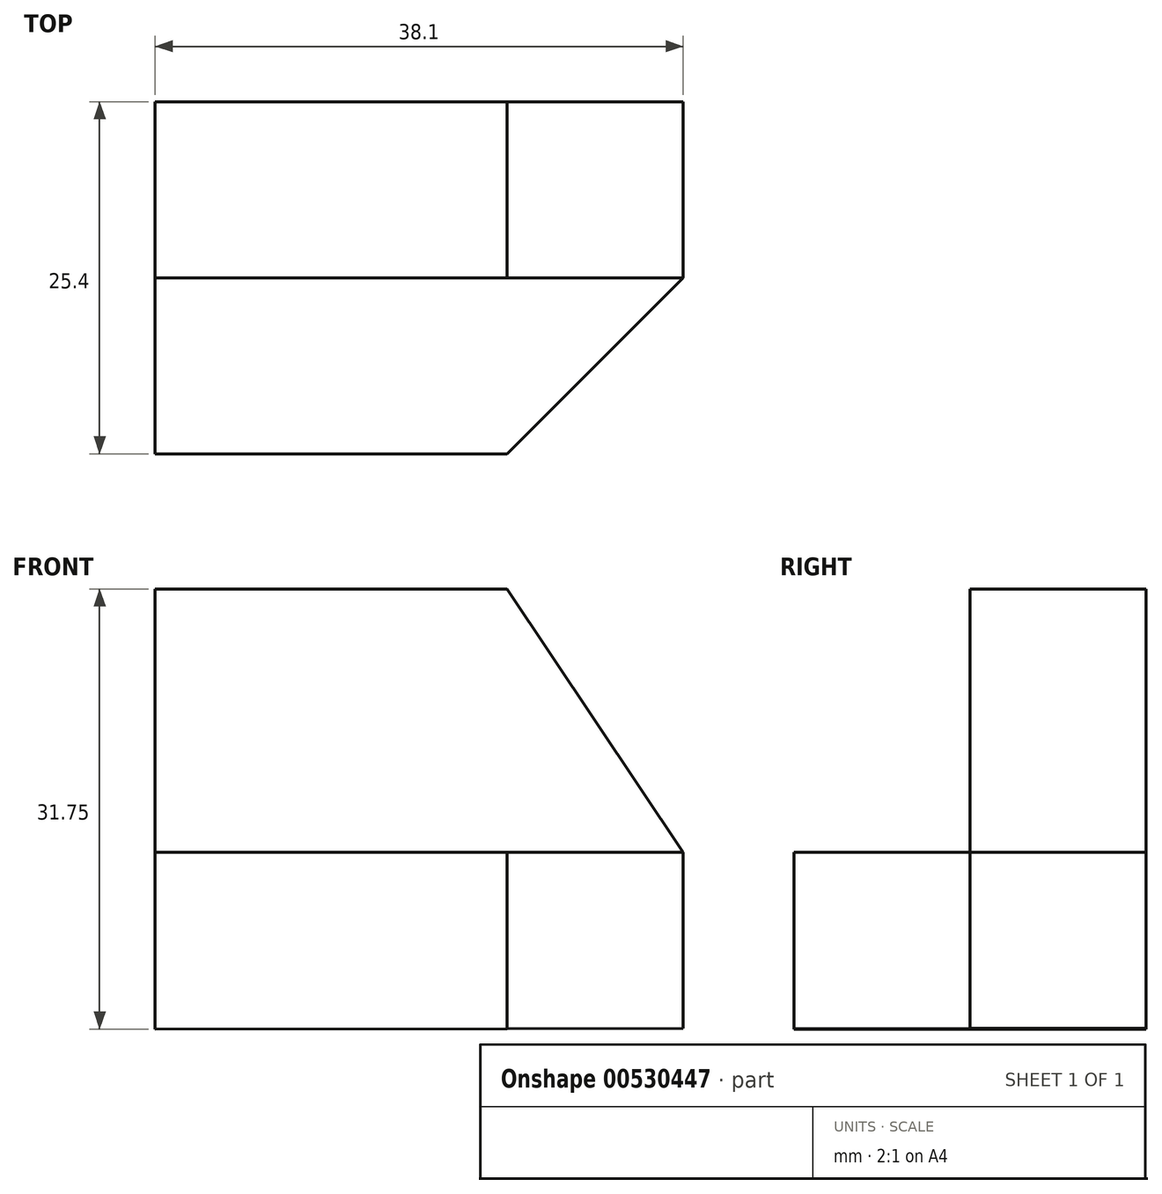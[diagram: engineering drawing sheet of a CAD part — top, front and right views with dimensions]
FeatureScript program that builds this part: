
annotation { "Feature Type Name" : "Feature", "Feature Type Description" : "" }
export const myFeature = defineFeature(function(context is Context, id is Id, definition is map)
    precondition{}
    {
        {
            var Q0;
            Q0=qCreatedBy(makeId("Front.planeOp"),FACE);
            var sketch = newSketch(context, id + "F0", { "sketchPlane" : qUnion([Q0])});
            skLineSegment(sketch, "E0", {"start": v(-69.66, 61.41) * mm, "end": v(-69.66, 29.66) * mm});
            skLineSegment(sketch, "E1", {"start": v(-69.66, 61.41) * mm, "end": v(-44.26, 61.41) * mm});
            skLineSegment(sketch, "E2", {"start": v(-44.26, 61.41) * mm, "end": v(-31.56, 42.4) * mm});
            skLineSegment(sketch, "E3", {"start": v(-31.56, 42.4) * mm, "end": v(-31.56, 29.7) * mm});
            skLineSegment(sketch, "E4", {"start": v(-31.56, 29.7) * mm, "end": v(-69.66, 29.66) * mm});
            skSolve(sketch);
        }
        {
            var Q0;
            Q0=makeQuery(id+"FoG6RG5lKM2hwuI_0.opExtrude","CAP_FACE",FACE,{"disambiguationData":[OSD([sQuery(id+"F0.wireOp",EDGE,"E0"),sQuery(id+"F0.wireOp",EDGE,"E1"),sQuery(id+"F0.wireOp",EDGE,"E2"),sQuery(id+"F0.wireOp",EDGE,"E3"),sQuery(id+"F0.wireOp",EDGE,"E4")])],"isStart":false});
            var sketch = newSketch(context, id + "F1", { "sketchPlane" : qUnion([Q0])});
            skLineSegment(sketch, "E5", {"start": v(-31.56, 29.7) * mm, "end": v(-31.56, 42.4) * mm});
            skLineSegment(sketch, "E6", {"start": v(-31.56, 42.4) * mm, "end": v(-69.66, 42.4) * mm});
            skLineSegment(sketch, "E7", {"start": v(-69.66, 42.4) * mm, "end": v(-69.66, 29.66) * mm});
            skLineSegment(sketch, "E8", {"start": v(-69.66, 29.66) * mm, "end": v(-31.56, 29.7) * mm});
            skSolve(sketch);
        }
        {
            var Q0;
            Q0=makeQuery(id+"FJzksTEYq52pJHC_0.opExtrude","CAP_FACE",FACE,{"disambiguationData":[OSD([sQuery(id+"F0.wireOp",EDGE,"E0"),sQuery(id+"F0.wireOp",EDGE,"E1"),sQuery(id+"F0.wireOp",EDGE,"E2"),sQuery(id+"F0.wireOp",EDGE,"E3"),sQuery(id+"F0.wireOp",EDGE,"E4")])],"isStart":false});
            var sketch = newSketch(context, id + "F2", { "sketchPlane" : qUnion([Q0])});
            skLineSegment(sketch, "E9", {"start": v(-69.66, 29.66) * mm, "end": v(-31.56, 29.7) * mm});
            skLineSegment(sketch, "E10", {"start": v(-31.56, 29.7) * mm, "end": v(-31.56, 42.4) * mm});
            skLineSegment(sketch, "E11", {"start": v(-31.56, 42.4) * mm, "end": v(-69.66, 42.4) * mm});
            skLineSegment(sketch, "E12", {"start": v(-69.66, 42.4) * mm, "end": v(-69.66, 29.66) * mm});
            skSolve(sketch);
        }
        {
            var Q0;
            Q0=makeQuery(id+"F0.imprint","IMPRINT",FACE,{"disambiguationData":[TD([[makeQuery(id+"F0.imprint","IMPRINT",EDGE,{"derivedFrom":sQuery(id+"F0.wireOp",EDGE,"E0")}),1.0]])]});
            extrude(context, id + "F3", {"entities" : qUnion([Q0]), "depth" : 12.7 * mm, "offsetDistance" : 25.4 * mm});
        }
        {
            var Q0;
            Q0=makeQuery(id+"F3.opExtrude","CAP_FACE",FACE,{"disambiguationData":[OSD([sQuery(id+"F0.wireOp",EDGE,"E0"),sQuery(id+"F0.wireOp",EDGE,"E1"),sQuery(id+"F0.wireOp",EDGE,"E2"),sQuery(id+"F0.wireOp",EDGE,"E3"),sQuery(id+"F0.wireOp",EDGE,"E4")])],"isStart":false});
            var sketch = newSketch(context, id + "F4", { "sketchPlane" : qUnion([Q0])});
            skLineSegment(sketch, "E13", {"start": v(-69.66, 29.66) * mm, "end": v(-31.56, 29.7) * mm});
            skLineSegment(sketch, "E14", {"start": v(-31.56, 29.7) * mm, "end": v(-31.56, 42.4) * mm});
            skLineSegment(sketch, "E15", {"start": v(-31.56, 42.4) * mm, "end": v(-69.66, 42.4) * mm});
            skLineSegment(sketch, "E16", {"start": v(-69.66, 42.4) * mm, "end": v(-69.66, 29.66) * mm});
            skSolve(sketch);
        }
        {
            var Q0;
            Q0=makeQuery(id+"F4.imprint","IMPRINT",FACE,{"disambiguationData":[TD([[makeQuery(id+"F4.imprint","IMPRINT",EDGE,{"derivedFrom":sQuery(id+"F4.wireOp",EDGE,"E13")}),-1.0]])]});
            extrude(context, id + "F5", {"entities" : qUnion([Q0]), "operationType" : NewBodyOperationType.ADD, "depth" : 12.7 * mm, "offsetDistance" : 25.4 * mm});
        }
        {
            var Q0;
            Q0=makeQuery(id+"F5.opExtrude","SWEPT_FACE",FACE,{"disambiguationData":[OSD([sQuery(id+"F4.wireOp",EDGE,"E15")])]});
            var sketch = newSketch(context, id + "F6", { "sketchPlane" : qUnion([Q0])});
            skLineSegment(sketch, "E17", {"start": v(-31.56, -12.7) * mm, "end": v(-44.26, -25.4) * mm});
            skSolve(sketch);
        }
        {
            var Q0;
            {var subQ0=sQuery(id+"F6.wireOp",EDGE,"E17");Q0=makeQuery(id+"F6.imprint","IMPRINT",FACE,{"disambiguationData":[TD([[makeQuery(id+"F6.imprint","IMPRINT",EDGE,{"derivedFrom":subQ0}),1.0]])]});}
            extrude(context, id + "F7", {"entities" : qUnion([Q0]), "operationType" : NewBodyOperationType.REMOVE, "endBound" : BoundingType.THROUGH_ALL, "oppositeDirection" : true, "depth" : 25.4 * mm, "offsetDistance" : 25.4 * mm});
        }
    });
